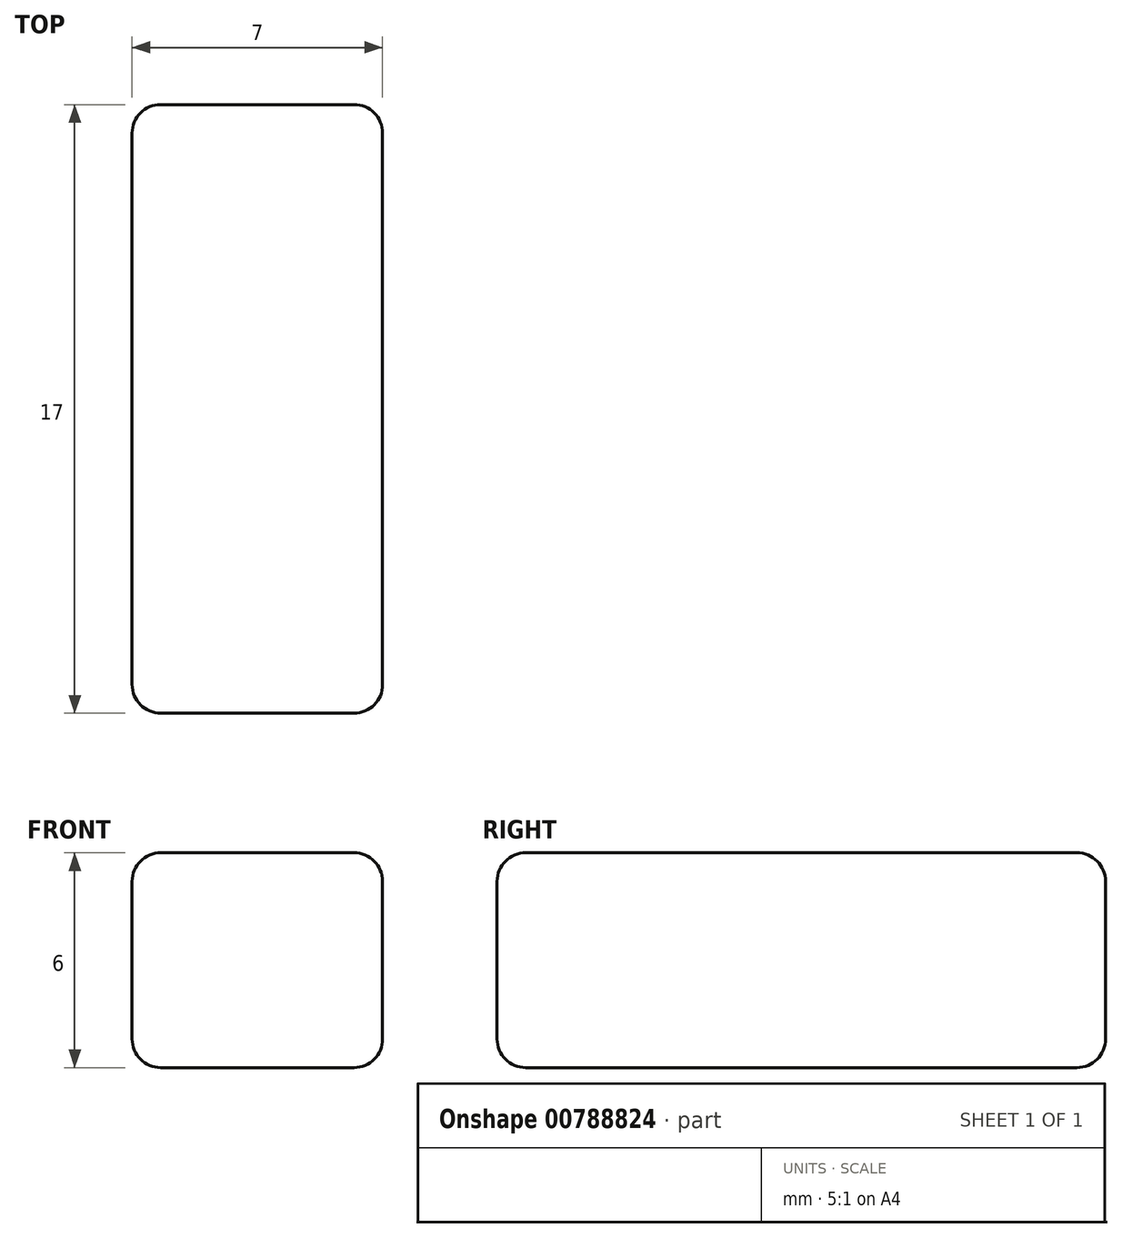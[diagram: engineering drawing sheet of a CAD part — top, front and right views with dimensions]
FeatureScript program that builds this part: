
annotation { "Feature Type Name" : "Feature", "Feature Type Description" : "" }
export const myFeature = defineFeature(function(context is Context, id is Id, definition is map)
    precondition{}
    {
        {
            var Q0;
            Q0=qCreatedBy(makeId("Top.planeOp"),FACE);
            var sketch = newSketch(context, id + "F0", { "sketchPlane" : qUnion([Q0])});
            skLineSegment(sketch, "E0.bottom", {"start": v(-3.5, 8.5) * mm, "end": v(3.5, 8.5) * mm});
            skLineSegment(sketch, "E0.top", {"start": v(-3.5, -8.5) * mm, "end": v(3.5, -8.5) * mm});
            skLineSegment(sketch, "E0.left", {"start": v(-3.5, 8.5) * mm, "end": v(-3.5, -8.5) * mm});
            skLineSegment(sketch, "E0.right", {"start": v(3.5, 8.5) * mm, "end": v(3.5, -8.5) * mm});
            skLineSegment(sketch, "E1", {"start": v(-3.5, 8.5) * mm, "end": v(3.5, -8.5) * mm, "construction": true});
            skSolve(sketch);
        }
        {
            var Q0;
            Q0 = qSketchRegion(id + "F0", true);
            extrude(context, id + "F1", {"entities" : qUnion([Q0]), "depth" : 6 * mm, "offsetDistance" : 25 * mm});
        }
        {
            var Q0;
            Q0=makeQuery(id+"F1.opExtrude","CAP_FACE",FACE,{"disambiguationData":[OSD([sQuery(id+"F0.wireOp",EDGE,"E0.bottom"),sQuery(id+"F0.wireOp",EDGE,"E0.top"),sQuery(id+"F0.wireOp",EDGE,"E0.left"),sQuery(id+"F0.wireOp",EDGE,"E0.right")])],"isStart":false});
            var Q1;
            Q1=makeQuery(id+"F1.opExtrude","CAP_FACE",FACE,{"disambiguationData":[OSD([sQuery(id+"F0.wireOp",EDGE,"E0.bottom"),sQuery(id+"F0.wireOp",EDGE,"E0.top"),sQuery(id+"F0.wireOp",EDGE,"E0.left"),sQuery(id+"F0.wireOp",EDGE,"E0.right")])],"isStart":true});
            var Q2;
            Q2=makeQuery(id+"F1.opExtrude","SWEPT_FACE",FACE,{"disambiguationData":[OSD([sQuery(id+"F0.wireOp",EDGE,"E0.right")])]});
            var Q3;
            Q3=makeQuery(id+"F1.opExtrude","SWEPT_FACE",FACE,{"disambiguationData":[OSD([sQuery(id+"F0.wireOp",EDGE,"E0.bottom")])]});
            var Q4;
            Q4=makeQuery(id+"F1.opExtrude","SWEPT_FACE",FACE,{"disambiguationData":[OSD([sQuery(id+"F0.wireOp",EDGE,"E0.left")])]});
            fillet(context, id + "F2", {"entities" : qUnion([Q0, Q1, Q2, Q3, Q4]), "radius" : 0.8 * mm, "tangentPropagation" : true, "allowEdgeOverflow" : false});
        }
    });
